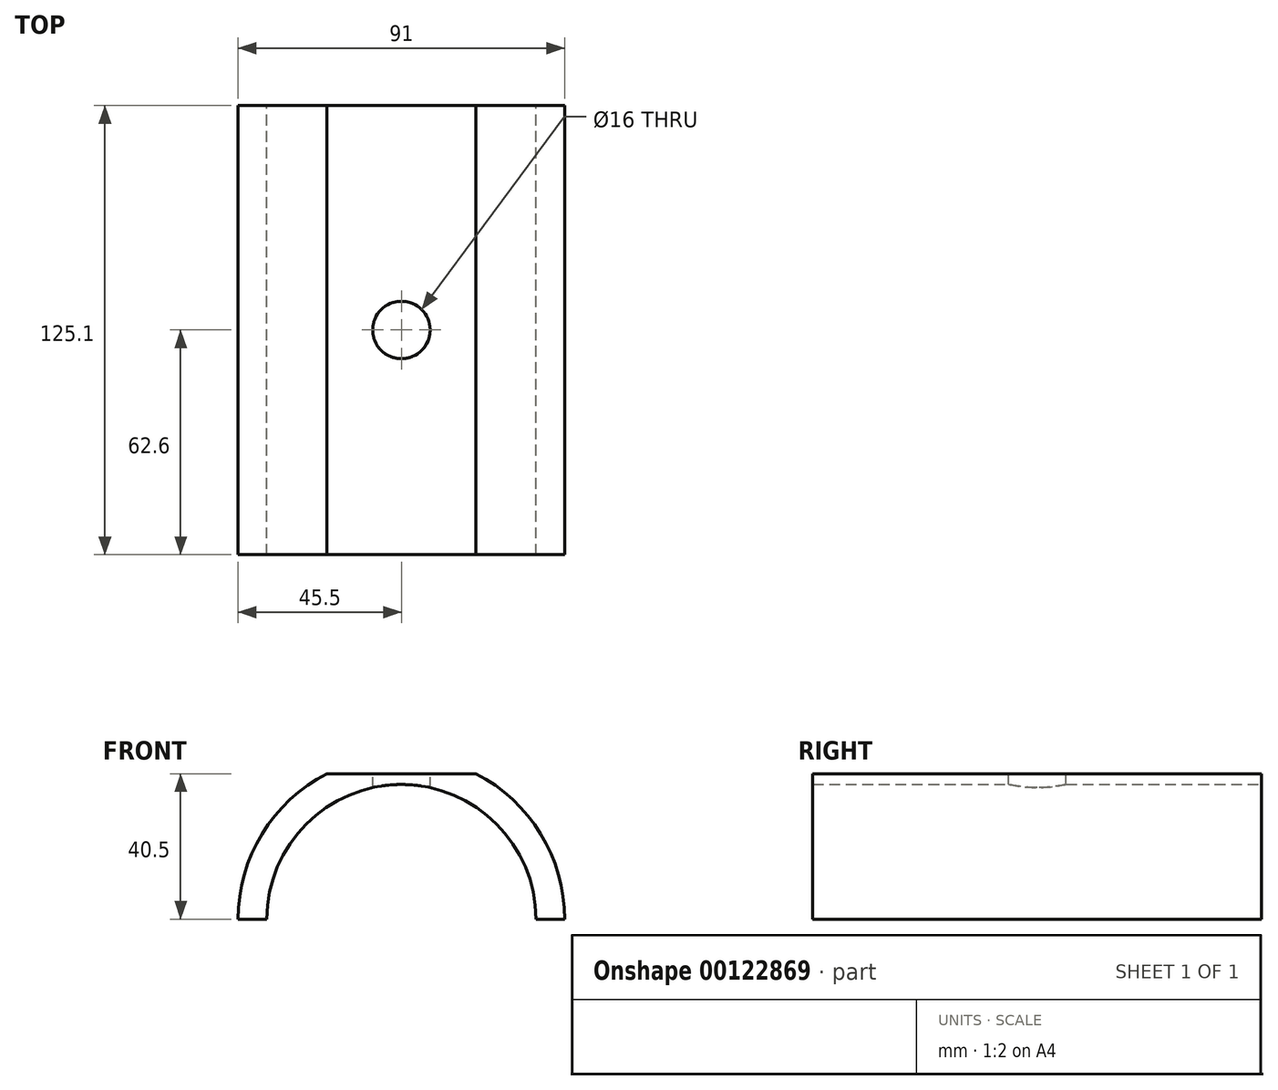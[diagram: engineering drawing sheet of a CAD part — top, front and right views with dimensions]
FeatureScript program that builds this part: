
annotation { "Feature Type Name" : "Feature", "Feature Type Description" : "" }
export const myFeature = defineFeature(function(context is Context, id is Id, definition is map)
    precondition{}
    {
        {
            var Q0;
            Q0=qCreatedBy(makeId("Front.planeOp"),FACE);
            var sketch = newSketch(context, id + "F0", { "sketchPlane" : qUnion([Q0])});
            skCircle(sketch, "E0", {"center": v(0, 0) * mm, "radius": 37.5 * mm});
            skCircle(sketch, "E1", {"center": v(0, 0) * mm, "radius": 45.5 * mm});
            skLineSegment(sketch, "E2", {"start": v(-45.5, 0) * mm, "end": v(45.5, 0) * mm});
            skSolve(sketch);
        }
        {
            var Q0;
            {var subQ0=sQuery(id+"F0.wireOp",EDGE,"E2");var subQ1=sQuery(id+"F0.wireOp",EDGE,"E0");var subQ2=makeQuery(id+"F0.imprint","INTERSECT",VERTEX,{"disambiguationData":[OD(0.0)],"derivedFrom":[subQ1,subQ0]});Q0=makeQuery(id+"F0.imprint","IMPRINT",FACE,{"disambiguationData":[TD([[makeQuery(id+"F0.imprint","IMPRINT",EDGE,{"disambiguationData":[TD([[subQ2,1.0]])],"derivedFrom":subQ1}),-1.0]])]});}
            extrude(context, id + "F1", {"entities" : qUnion([Q0]), "depth" : 125.1 * mm});
        }
        {
            var Q0;
            Q0=qCreatedBy(makeId("Front.planeOp"),FACE);
            var sketch = newSketch(context, id + "F2", { "sketchPlane" : qUnion([Q0])});
            skPoint(sketch, "E3", {"position": v(0, 40.5) * mm});
            skPoint(sketch, "E4", {"position": v(22, 40.5) * mm});
            skPoint(sketch, "E5", {"position": v(-22, 40.5) * mm});
            skLineSegment(sketch, "E6", {"start": v(-22, 40.5) * mm, "end": v(22, 40.5) * mm});
            skLineSegment(sketch, "E7", {"start": v(22, 48.87) * mm, "end": v(-22, 48.87) * mm});
            skLineSegment(sketch, "E8", {"start": v(-22, 48.87) * mm, "end": v(-22, 40.5) * mm});
            skLineSegment(sketch, "E9", {"start": v(22, 48.87) * mm, "end": v(22, 40.5) * mm});
            skSolve(sketch);
        }
        {
            var Q0;
            Q0=qSketchRegion(id+"F2",true);
            extrude(context, id + "F3", {"entities" : qUnion([Q0]), "operationType" : NewBodyOperationType.REMOVE, "depth" : 125.1 * mm});
        }
        {
            var Q0;
            Q0=makeQuery(id+"F3.boolean.opBoolean","COPY",FACE,{"derivedFrom":makeQuery(id+"F3.opExtrude","SWEPT_FACE",FACE,{"disambiguationData":[OSD([sQuery(id+"F2.wireOp",EDGE,"E6")])]})});
            var sketch = newSketch(context, id + "F4", { "sketchPlane" : qUnion([Q0])});
            skPoint(sketch, "E10", {"position": v(0, 0) * mm});
            skPoint(sketch, "E11", {"position": v(0, -62.5) * mm});
            skCircle(sketch, "E12", {"center": v(0, -62.5) * mm, "radius": 8 * mm});
            skSolve(sketch);
        }
        {
            var Q0;
            Q0=qSketchRegion(id+"F4",true);
            extrude(context, id + "F5", {"entities" : qUnion([Q0]), "operationType" : NewBodyOperationType.REMOVE, "oppositeDirection" : true, "depth" : 4 * mm});
        }
    });
